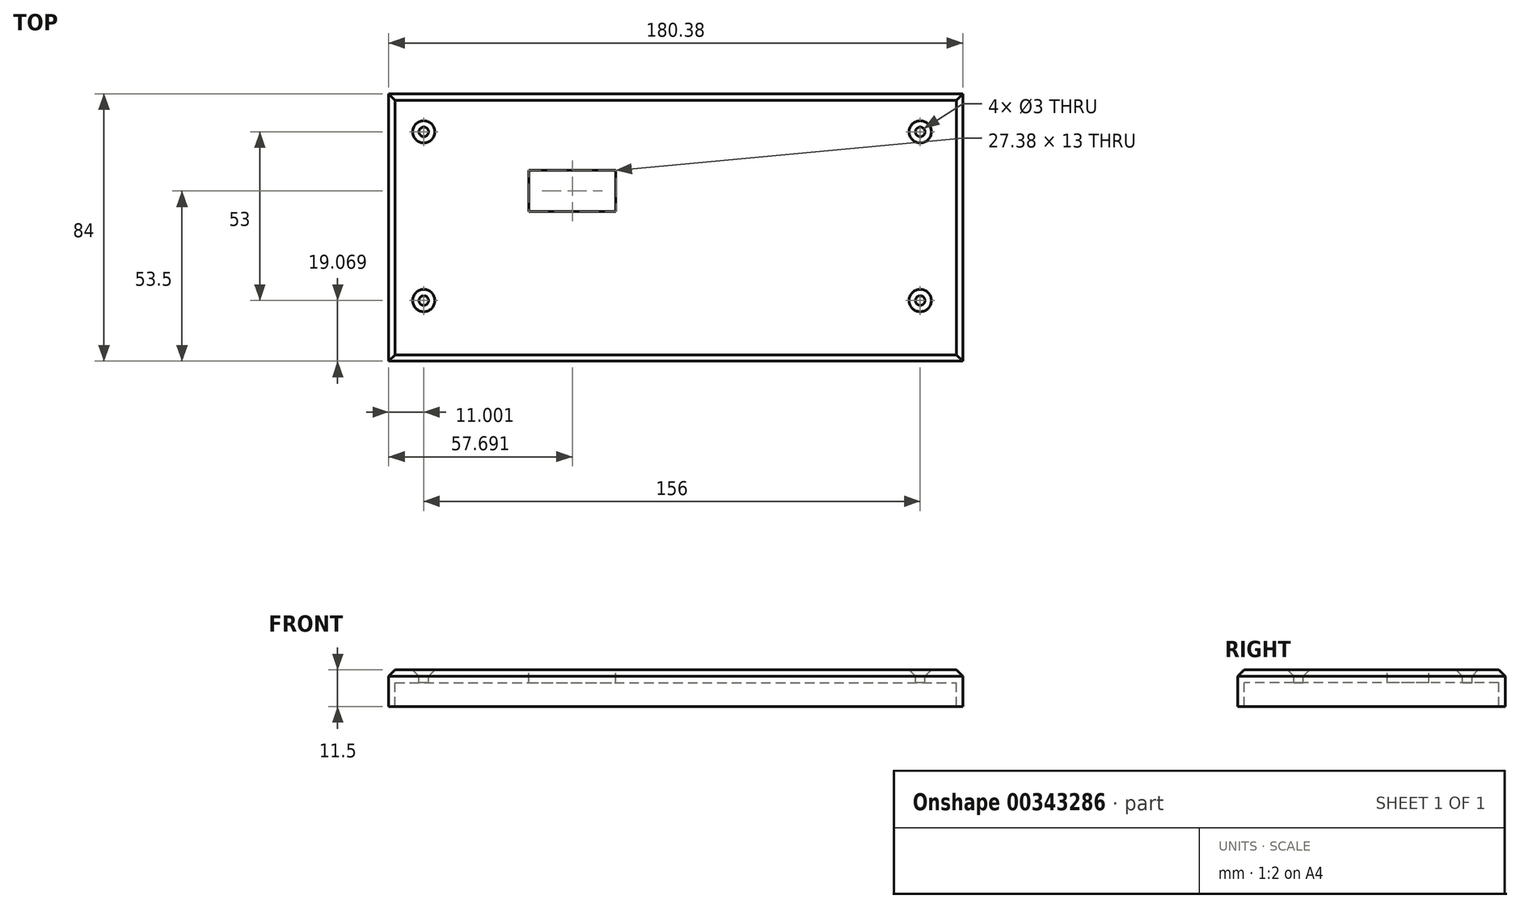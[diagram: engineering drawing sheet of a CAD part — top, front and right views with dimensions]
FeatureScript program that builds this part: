
annotation { "Feature Type Name" : "Feature", "Feature Type Description" : "" }
export const myFeature = defineFeature(function(context is Context, id is Id, definition is map)
    precondition{}
    {
        {
            var Q0;
            Q0=qCreatedBy(makeId("Top.planeOp"),FACE);
            var sketch = newSketch(context, id + "F0", { "sketchPlane" : qUnion([Q0])});
            skLineSegment(sketch, "E0.bottom", {"start": v(0, 0) * mm, "end": v(-180.38, 0) * mm});
            skLineSegment(sketch, "E0.top", {"start": v(0, 84) * mm, "end": v(-180.38, 84) * mm});
            skLineSegment(sketch, "E0.left", {"start": v(0, 0) * mm, "end": v(0, 84) * mm});
            skLineSegment(sketch, "E0.right", {"start": v(-180.38, 0) * mm, "end": v(-180.38, 84) * mm});
            skLineSegment(sketch, "E1.bottom", {"start": v(-163, 62.5) * mm, "end": v(-63, 62.5) * mm});
            skLineSegment(sketch, "E1.top", {"start": v(-163, 21.5) * mm, "end": v(-63, 21.5) * mm});
            skLineSegment(sketch, "E1.left", {"start": v(-163, 62.5) * mm, "end": v(-163, 21.5) * mm});
            skLineSegment(sketch, "E1.right", {"start": v(-63, 62.5) * mm, "end": v(-63, 21.5) * mm});
            skLineSegment(sketch, "E2.bottom", {"start": v(-178.38, 82) * mm, "end": v(-2, 82) * mm});
            skLineSegment(sketch, "E2.top", {"start": v(-178.38, 2) * mm, "end": v(-2, 2) * mm});
            skLineSegment(sketch, "E2.left", {"start": v(-178.38, 82) * mm, "end": v(-178.38, 2) * mm});
            skLineSegment(sketch, "E2.right", {"start": v(-2, 82) * mm, "end": v(-2, 2) * mm});
            skLineSegment(sketch, "E3.left", {"start": v(-63, 62.5) * mm, "end": v(-63, 14.27) * mm});
            skCircle(sketch, "E4", {"center": v(-35, 42) * mm, "radius": 5 * mm});
            skLineSegment(sketch, "E5", {"start": v(-35, 82) * mm, "end": v(-35, 2) * mm});
            skLineSegment(sketch, "E6", {"start": v(-35, 42) * mm, "end": v(-35, 58) * mm});
            skCircle(sketch, "E7", {"center": v(-35, 58) * mm, "radius": 5 * mm});
            skLineSegment(sketch, "E8", {"start": v(-35, 42) * mm, "end": v(-35, 26) * mm});
            skCircle(sketch, "E9", {"center": v(-35, 26) * mm, "radius": 5 * mm});
            skLineSegment(sketch, "E10", {"start": v(-63, 42) * mm, "end": v(0, 42) * mm});
            skCircle(sketch, "E11", {"center": v(-51, 42) * mm, "radius": 5 * mm});
            skCircle(sketch, "E12", {"center": v(-19, 42) * mm, "radius": 5 * mm});
            skLineSegment(sketch, "E13.bottom", {"start": v(-173.38, 76.07) * mm, "end": v(-9.38, 76.07) * mm});
            skLineSegment(sketch, "E13.top", {"start": v(-173.38, 15.07) * mm, "end": v(-9.38, 15.07) * mm});
            skLineSegment(sketch, "E13.left", {"start": v(-173.38, 76.07) * mm, "end": v(-173.38, 15.07) * mm});
            skLineSegment(sketch, "E13.right", {"start": v(-9.38, 76.07) * mm, "end": v(-9.38, 15.07) * mm});
            skCircle(sketch, "E14", {"center": v(-169.38, 19.07) * mm, "radius": 1.5 * mm});
            skCircle(sketch, "E15", {"center": v(-169.38, 72.07) * mm, "radius": 1.5 * mm});
            skCircle(sketch, "E16", {"center": v(-13.38, 72.07) * mm, "radius": 1.5 * mm});
            skCircle(sketch, "E17", {"center": v(-13.38, 19.07) * mm, "radius": 1.5 * mm});
            skSolve(sketch);
        }
        {
            var Q0;
            Q0 = qSketchRegion(id + "F0", true);
            extrude(context, id + "F1", {"entities" : qUnion([Q0]), "oppositeDirection" : true, "depth" : 11.5 * mm});
        }
        {
            var Q0;
            {var subQ5=sQuery(id+"F0.wireOp",EDGE,"E2.left");Q0=makeQuery(id+"F0.imprint","IMPRINT",FACE,{"disambiguationData":[TD([[makeQuery(id+"F0.imprint","IMPRINT",EDGE,{"derivedFrom":subQ5}),1.0]])]});}
            var Q1;
            {var subQ21=sQuery(id+"F0.wireOp",EDGE,"E1.bottom");Q1=makeQuery(id+"F0.imprint","IMPRINT",FACE,{"disambiguationData":[TD([[makeQuery(id+"F0.imprint","IMPRINT",EDGE,{"derivedFrom":subQ21}),1.0]])]});}
            var Q2;
            Q2=makeQuery(id+"F0.imprint","IMPRINT",FACE,{"disambiguationData":[TD([[makeQuery(id+"F0.imprint","IMPRINT",EDGE,{"derivedFrom":sQuery(id+"F0.wireOp",EDGE,"E16")}),-1.0]])]});
            var Q3;
            {var subQ1=sQuery(id+"F0.wireOp",EDGE,"E2.bottom");var subQ6=sQuery(id+"F0.wireOp",EDGE,"E2.right");var subQ10=makeQuery(id+"F0.imprint","INTERSECT",VERTEX,{"derivedFrom":[subQ1,subQ6]});Q3=makeQuery(id+"F0.imprint","IMPRINT",FACE,{"disambiguationData":[TD([[makeQuery(id+"F0.imprint","IMPRINT",EDGE,{"disambiguationData":[TD([[subQ10,1.0]])],"derivedFrom":subQ1}),-1.0]])]});}
            var Q4;
            {var subQ1=sQuery(id+"F0.wireOp",EDGE,"E2.right");var subQ7=sQuery(id+"F0.wireOp",EDGE,"E2.top");var subQ8=makeQuery(id+"F0.imprint","INTERSECT",VERTEX,{"derivedFrom":[subQ7,subQ1]});Q4=makeQuery(id+"F0.imprint","IMPRINT",FACE,{"disambiguationData":[TD([[makeQuery(id+"F0.imprint","IMPRINT",EDGE,{"disambiguationData":[TD([[subQ8,1.0]])],"derivedFrom":subQ7}),1.0]])]});}
            var Q5;
            Q5=makeQuery(id+"F0.imprint","IMPRINT",FACE,{"disambiguationData":[TD([[makeQuery(id+"F0.imprint","IMPRINT",EDGE,{"derivedFrom":sQuery(id+"F0.wireOp",EDGE,"E17")}),-1.0]])]});
            var Q6;
            {var subQ5=sQuery(id+"F0.wireOp",EDGE,"E3.left");var subQ6=makeQuery(id+"F0.imprint","INTERSECT",VERTEX,{"derivedFrom":[sQuery(id+"F0.wireOp",EDGE,"E1.top"),subQ5]});Q6=makeQuery(id+"F0.imprint","IMPRINT",FACE,{"disambiguationData":[TD([[makeQuery(id+"F0.imprint","IMPRINT",EDGE,{"disambiguationData":[TD([[subQ6,1.0]])],"derivedFrom":subQ5}),1.0]])]});}
            var Q7;
            {var subQ0=sQuery(id+"F0.wireOp",EDGE,"E11");var subQ1=sQuery(id+"F0.wireOp",EDGE,"E10");var subQ2=makeQuery(id+"F0.imprint","INTERSECT",VERTEX,{"disambiguationData":[OD(0.0)],"derivedFrom":[subQ1,subQ0]});Q7=makeQuery(id+"F0.imprint","IMPRINT",FACE,{"disambiguationData":[TD([[makeQuery(id+"F0.imprint","IMPRINT",EDGE,{"disambiguationData":[TD([[subQ2,-1.0]])],"derivedFrom":subQ1}),-1.0]])]});}
            var Q8;
            {var subQ0=sQuery(id+"F0.wireOp",EDGE,"E11");var subQ1=sQuery(id+"F0.wireOp",EDGE,"E10");var subQ2=makeQuery(id+"F0.imprint","INTERSECT",VERTEX,{"disambiguationData":[OD(0.0)],"derivedFrom":[subQ1,subQ0]});Q8=makeQuery(id+"F0.imprint","IMPRINT",FACE,{"disambiguationData":[TD([[makeQuery(id+"F0.imprint","IMPRINT",EDGE,{"disambiguationData":[TD([[subQ2,-1.0]])],"derivedFrom":subQ1}),1.0]])]});}
            var Q9;
            {var subQ0=sQuery(id+"F0.wireOp",EDGE,"E10");var subQ1=sQuery(id+"F0.wireOp",EDGE,"E4");var subQ2=makeQuery(id+"F0.imprint","INTERSECT",VERTEX,{"disambiguationData":[OD(0.0)],"derivedFrom":[subQ1,subQ0]});Q9=makeQuery(id+"F0.imprint","IMPRINT",FACE,{"disambiguationData":[TD([[makeQuery(id+"F0.imprint","IMPRINT",EDGE,{"disambiguationData":[TD([[subQ2,1.0]])],"derivedFrom":subQ1}),1.0]])]});}
            var Q10;
            {var subQ0=sQuery(id+"F0.wireOp",EDGE,"E6");var subQ1=sQuery(id+"F0.wireOp",EDGE,"E4");var subQ2=makeQuery(id+"F0.imprint","INTERSECT",VERTEX,{"derivedFrom":[subQ1,subQ0]});Q10=makeQuery(id+"F0.imprint","IMPRINT",FACE,{"disambiguationData":[TD([[makeQuery(id+"F0.imprint","IMPRINT",EDGE,{"disambiguationData":[TD([[subQ2,1.0]])],"derivedFrom":subQ1}),1.0]])]});}
            var Q11;
            {var subQ0=sQuery(id+"F0.wireOp",EDGE,"E10");var subQ1=sQuery(id+"F0.wireOp",EDGE,"E4");var subQ2=makeQuery(id+"F0.imprint","INTERSECT",VERTEX,{"disambiguationData":[OD(1.0)],"derivedFrom":[subQ1,subQ0]});Q11=makeQuery(id+"F0.imprint","IMPRINT",FACE,{"disambiguationData":[TD([[makeQuery(id+"F0.imprint","IMPRINT",EDGE,{"disambiguationData":[TD([[subQ2,-1.0]])],"derivedFrom":subQ1}),1.0]])]});}
            var Q12;
            {var subQ0=sQuery(id+"F0.wireOp",EDGE,"E6");var subQ1=sQuery(id+"F0.wireOp",EDGE,"E4");var subQ2=makeQuery(id+"F0.imprint","INTERSECT",VERTEX,{"derivedFrom":[subQ1,subQ0]});Q12=makeQuery(id+"F0.imprint","IMPRINT",FACE,{"disambiguationData":[TD([[makeQuery(id+"F0.imprint","IMPRINT",EDGE,{"disambiguationData":[TD([[subQ2,-1.0]])],"derivedFrom":subQ1}),1.0]])]});}
            var Q13;
            {var subQ0=sQuery(id+"F0.wireOp",EDGE,"E12");var subQ1=sQuery(id+"F0.wireOp",EDGE,"E10");var subQ2=makeQuery(id+"F0.imprint","INTERSECT",VERTEX,{"disambiguationData":[OD(0.0)],"derivedFrom":[subQ1,subQ0]});Q13=makeQuery(id+"F0.imprint","IMPRINT",FACE,{"disambiguationData":[TD([[makeQuery(id+"F0.imprint","IMPRINT",EDGE,{"disambiguationData":[TD([[subQ2,-1.0]])],"derivedFrom":subQ1}),-1.0]])]});}
            var Q14;
            {var subQ0=sQuery(id+"F0.wireOp",EDGE,"E12");var subQ1=sQuery(id+"F0.wireOp",EDGE,"E10");var subQ2=makeQuery(id+"F0.imprint","INTERSECT",VERTEX,{"disambiguationData":[OD(0.0)],"derivedFrom":[subQ1,subQ0]});Q14=makeQuery(id+"F0.imprint","IMPRINT",FACE,{"disambiguationData":[TD([[makeQuery(id+"F0.imprint","IMPRINT",EDGE,{"disambiguationData":[TD([[subQ2,-1.0]])],"derivedFrom":subQ1}),1.0]])]});}
            var Q15;
            {var subQ0=sQuery(id+"F0.wireOp",EDGE,"E6");var subQ1=sQuery(id+"F0.wireOp",EDGE,"E5");var subQ2=makeQuery(id+"F0.imprint","INTERSECT",VERTEX,{"derivedFrom":[subQ1,subQ0]});Q15=makeQuery(id+"F0.imprint","IMPRINT",FACE,{"disambiguationData":[TD([[makeQuery(id+"F0.imprint","IMPRINT",EDGE,{"disambiguationData":[TD([[subQ2,1.0]])],"derivedFrom":subQ1}),1.0]])]});}
            var Q16;
            {var subQ0=sQuery(id+"F0.wireOp",EDGE,"E6");var subQ1=sQuery(id+"F0.wireOp",EDGE,"E5");var subQ2=makeQuery(id+"F0.imprint","INTERSECT",VERTEX,{"derivedFrom":[subQ1,subQ0]});Q16=makeQuery(id+"F0.imprint","IMPRINT",FACE,{"disambiguationData":[TD([[makeQuery(id+"F0.imprint","IMPRINT",EDGE,{"disambiguationData":[TD([[subQ2,1.0]])],"derivedFrom":subQ1}),-1.0]])]});}
            var Q17;
            {var subQ0=sQuery(id+"F0.wireOp",EDGE,"E8");var subQ1=sQuery(id+"F0.wireOp",EDGE,"E5");var subQ2=makeQuery(id+"F0.imprint","INTERSECT",VERTEX,{"derivedFrom":[subQ1,subQ0]});Q17=makeQuery(id+"F0.imprint","IMPRINT",FACE,{"disambiguationData":[TD([[makeQuery(id+"F0.imprint","IMPRINT",EDGE,{"disambiguationData":[TD([[subQ2,-1.0]])],"derivedFrom":subQ1}),1.0]])]});}
            var Q18;
            {var subQ0=sQuery(id+"F0.wireOp",EDGE,"E8");var subQ1=sQuery(id+"F0.wireOp",EDGE,"E5");var subQ2=makeQuery(id+"F0.imprint","INTERSECT",VERTEX,{"derivedFrom":[subQ1,subQ0]});Q18=makeQuery(id+"F0.imprint","IMPRINT",FACE,{"disambiguationData":[TD([[makeQuery(id+"F0.imprint","IMPRINT",EDGE,{"disambiguationData":[TD([[subQ2,-1.0]])],"derivedFrom":subQ1}),-1.0]])]});}
            var Q19;
            {var subQ2=sQuery(id+"F0.wireOp",EDGE,"E1.bottom");Q19=makeQuery(id+"F0.imprint","IMPRINT",FACE,{"disambiguationData":[TD([[makeQuery(id+"F0.imprint","IMPRINT",EDGE,{"derivedFrom":subQ2}),-1.0]])]});}
            var Q20;
            Q20 = qSketchRegion(id + "F4", true);
            extrude(context, id + "F2", {"entities" : qUnion([Q0, Q1, Q2, Q3, Q4, Q5, Q6, Q7, Q8, Q9, Q10, Q11, Q12, Q13, Q14, Q15, Q16, Q17, Q18, Q19, Q20]), "operationType" : NewBodyOperationType.ADD, "oppositeDirection" : true, "depth" : 4 * mm});
        }
        {
            var Q0;
            Q0=makeQuery(id+"F1.opExtrude","CAP_EDGE",EDGE,{"disambiguationData":[OSD([sQuery(id+"F0.wireOp",EDGE,"E0.top")])],"isStart":true});
            var Q1;
            Q1=makeQuery(id+"F1.opExtrude","CAP_EDGE",EDGE,{"disambiguationData":[OSD([sQuery(id+"F0.wireOp",EDGE,"E0.left")])],"isStart":true});
            var Q2;
            Q2=makeQuery(id+"F1.opExtrude","CAP_EDGE",EDGE,{"disambiguationData":[OSD([sQuery(id+"F0.wireOp",EDGE,"E0.bottom")])],"isStart":true});
            var Q3;
            {var subQ0=sQuery(id+"F0.wireOp",EDGE,"E2.right");var subQ1=sQuery(id+"F0.wireOp",EDGE,"E2.left");var subQ2=sQuery(id+"F0.wireOp",EDGE,"E2.top");var subQ3=sQuery(id+"F0.wireOp",EDGE,"E2.bottom");Q3=makeQuery(id+"F2.boolean.opBoolean","MERGE",FACE,{"derivedFrom":[makeQuery(id+"F1.opExtrude","CAP_FACE",FACE,{"disambiguationData":[OSD([sQuery(id+"F0.wireOp",EDGE,"E0.bottom"),sQuery(id+"F0.wireOp",EDGE,"E0.top"),sQuery(id+"F0.wireOp",EDGE,"E0.left"),sQuery(id+"F0.wireOp",EDGE,"E0.right"),subQ3,subQ2,subQ1,subQ0])],"isStart":true}),makeQuery(id+"F2.opExtrude","CAP_FACE",FACE,{"disambiguationData":[OSD([sQuery(id+"F0.wireOp",EDGE,"G6Uh41Xb-bsXL-B4Dk-5VBm-K2apC45DesAB"),sQuery(id+"F0.wireOp",EDGE,"r5WoVds9-TPzW-YKKT-Vbkc-UcZyhsuEz2kt"),sQuery(id+"F0.wireOp",EDGE,"KEAikeoN-qBEB-nXGi-NRpe-0zCGGBcDTDKF"),sQuery(id+"F0.wireOp",EDGE,"iPMGfz6K-P6EP-grpC-2sPp-72670pLIPzsg"),sQuery(id+"F0.wireOp",EDGE,"E1.bottom"),sQuery(id+"F0.wireOp",EDGE,"E1.top"),sQuery(id+"F0.wireOp",EDGE,"E1.left"),subQ3,subQ2,subQ1,subQ0,sQuery(id+"F0.wireOp",EDGE,"E3.left"),sQuery(id+"F0.wireOp",EDGE,"E4"),sQuery(id+"F0.wireOp",EDGE,"E7"),sQuery(id+"F0.wireOp",EDGE,"E9"),sQuery(id+"F0.wireOp",EDGE,"E11"),sQuery(id+"F0.wireOp",EDGE,"E12")])],"isStart":true})]});}
            chamfer(context, id + "F3", {"entities" : qUnion([Q0, Q1, Q2, Q3]), "width" : 2 * mm, "tangentPropagation" : true});
        }
        {
            var Q0;
            {var subQ15=sQuery(id+"F0.wireOp",EDGE,"E1.bottom");Q0=makeQuery(id+"F0.imprint","IMPRINT",FACE,{"disambiguationData":[TD([[makeQuery(id+"F0.imprint","IMPRINT",EDGE,{"derivedFrom":subQ15}),1.0]])]});}
            var sketch = newSketch(context, id + "F4", { "sketchPlane" : qUnion([Q0])});
            skLineSegment(sketch, "E18.bottom", {"start": v(-136.38, 60) * mm, "end": v(-109, 60) * mm});
            skLineSegment(sketch, "E18.top", {"start": v(-136.38, 47) * mm, "end": v(-109, 47) * mm});
            skLineSegment(sketch, "E18.left", {"start": v(-136.38, 60) * mm, "end": v(-136.38, 47) * mm});
            skLineSegment(sketch, "E18.right", {"start": v(-109, 60) * mm, "end": v(-109, 47) * mm});
            skSolve(sketch);
        }
        {
            var Q0;
            Q0 = qSketchRegion(id + "F4", true);
            extrude(context, id + "F5", {"entities" : qUnion([Q0]), "operationType" : NewBodyOperationType.REMOVE, "oppositeDirection" : true, "depth" : 25 * mm});
        }
    });
